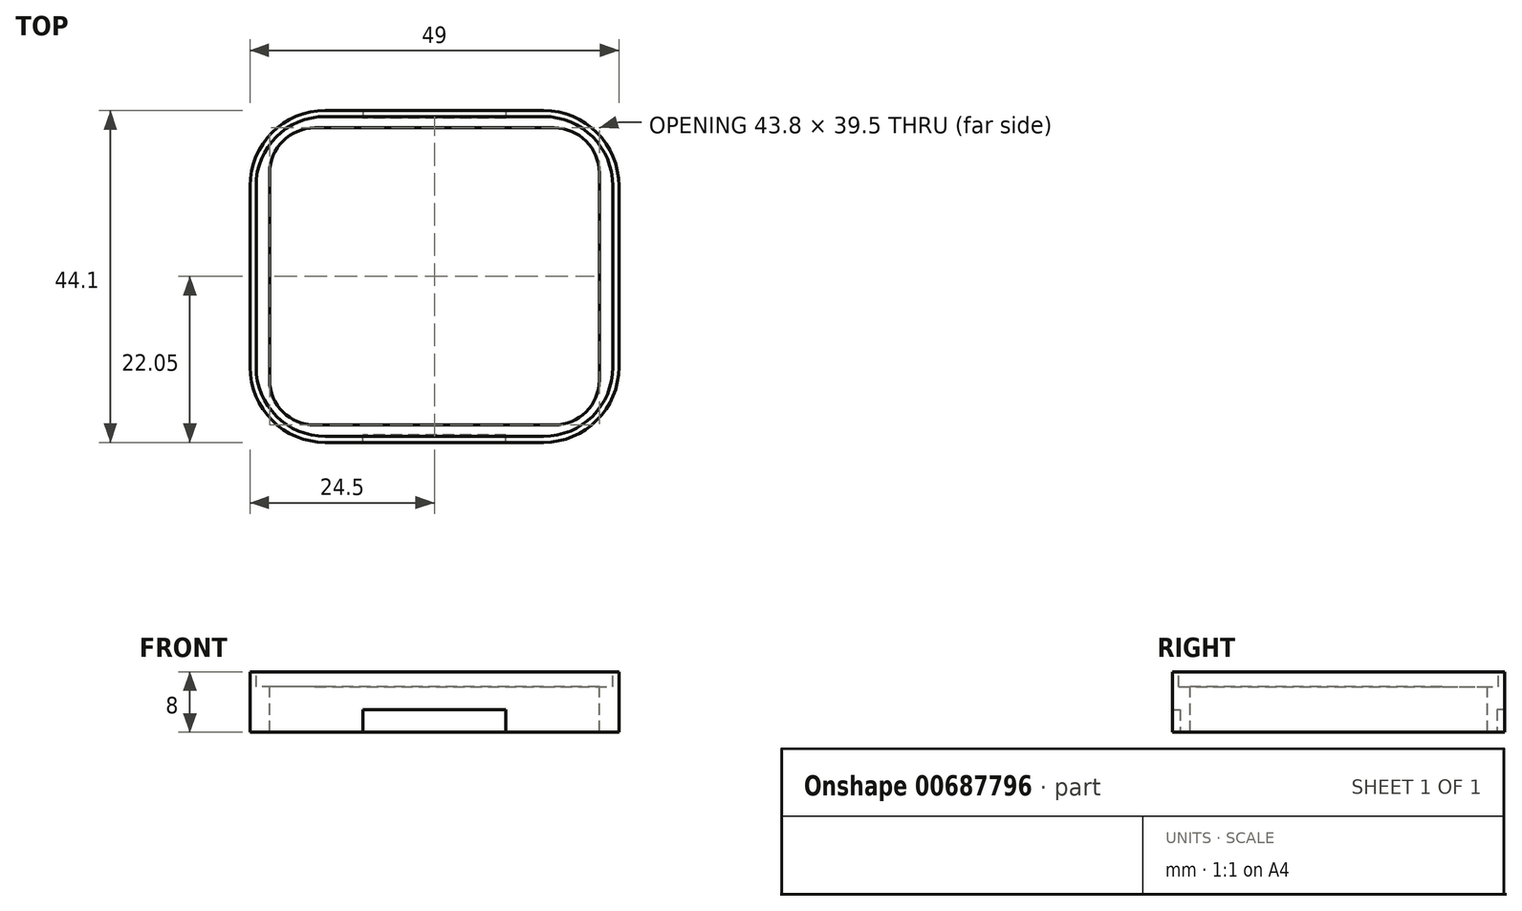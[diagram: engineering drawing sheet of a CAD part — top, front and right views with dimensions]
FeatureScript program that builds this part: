
annotation { "Feature Type Name" : "Feature", "Feature Type Description" : "" }
export const myFeature = defineFeature(function(context is Context, id is Id, definition is map)
    precondition{}
    {
        {
            var Q0;
            Q0=qCreatedBy(makeId("Top.planeOp"),FACE);
            var sketch = newSketch(context, id + "F0", { "sketchPlane" : qUnion([Q0])});
            skLineSegment(sketch, "E0.bottom", {"start": v(14.5, -22.05) * mm, "end": v(-14.5, -22.05) * mm});
            skLineSegment(sketch, "E0.top", {"start": v(14.5, 22.05) * mm, "end": v(-14.5, 22.05) * mm});
            skLineSegment(sketch, "E0.left", {"start": v(24.5, -12.05) * mm, "end": v(24.5, 12.05) * mm});
            skLineSegment(sketch, "E0.right", {"start": v(-24.5, -12.05) * mm, "end": v(-24.5, 12.05) * mm});
            skPoint(sketch, "E0.middle", {"position": v(0, 0) * mm});
            skPoint(sketch, "E1.visualSharp", {"position": v(-24.5, 22.05) * mm});
            skArc(sketch, "E1.filletArc", {"start": v(-14.5, 22.05) * mm, "mid": v(-21.57, 19.12) * mm, "end": v(-24.5, 12.05) * mm});
            skPoint(sketch, "E2.visualSharp", {"position": v(24.5, 22.05) * mm});
            skArc(sketch, "E2.filletArc", {"start": v(24.5, 12.05) * mm, "mid": v(21.57, 19.12) * mm, "end": v(14.5, 22.05) * mm});
            skPoint(sketch, "E3.visualSharp", {"position": v(24.5, -22.05) * mm});
            skArc(sketch, "E3.filletArc", {"start": v(14.5, -22.05) * mm, "mid": v(21.57, -19.12) * mm, "end": v(24.5, -12.05) * mm});
            skPoint(sketch, "E4.visualSharp", {"position": v(-24.5, -22.05) * mm});
            skArc(sketch, "E4.filletArc", {"start": v(-24.5, -12.05) * mm, "mid": v(-21.57, -19.12) * mm, "end": v(-14.5, -22.05) * mm});
            skSolve(sketch);
        }
        {
            var Q0;
            Q0=makeQuery(id+"F0.imprint","IMPRINT",FACE,{"disambiguationData":[TD([[makeQuery(id+"F0.imprint","IMPRINT",EDGE,{"derivedFrom":sQuery(id+"F0.wireOp",EDGE,"E0.bottom")}),-1.0]])]});
            var Q1;
            Q1=sQuery(id+"F0.wireOp",EDGE,"E0.top");
            var Q2;
            Q2=sQuery(id+"F0.wireOp",EDGE,"E1.filletArc");
            var Q3;
            Q3=sQuery(id+"F0.wireOp",EDGE,"E0.right");
            var Q4;
            Q4=sQuery(id+"F0.wireOp",EDGE,"E4.filletArc");
            var Q5;
            Q5=sQuery(id+"F0.wireOp",EDGE,"E0.bottom");
            var Q6;
            Q6=sQuery(id+"F0.wireOp",EDGE,"E3.filletArc");
            var Q7;
            Q7=sQuery(id+"F0.wireOp",EDGE,"E2.filletArc");
            var Q8;
            Q8=sQuery(id+"F0.wireOp",EDGE,"E0.left");
            extrude(context, id + "F1", {"entities" : qUnion([Q0]), "surfaceEntities" : qUnion([Q1, Q2, Q3, Q4, Q5, Q6, Q7, Q8]), "depth" : 8 * mm, "offsetDistance" : 25 * mm});
        }
        {
            var Q0;
            Q0=makeQuery(id+"F1.opExtrude","CAP_FACE",FACE,{"disambiguationData":[OSD([sQuery(id+"F0.wireOp",EDGE,"E0.bottom"),sQuery(id+"F0.wireOp",EDGE,"E0.top"),sQuery(id+"F0.wireOp",EDGE,"E0.left"),sQuery(id+"F0.wireOp",EDGE,"E0.right"),sQuery(id+"F0.wireOp",EDGE,"E1.filletArc"),sQuery(id+"F0.wireOp",EDGE,"E2.filletArc"),sQuery(id+"F0.wireOp",EDGE,"E3.filletArc"),sQuery(id+"F0.wireOp",EDGE,"E4.filletArc")])],"isStart":false});
            var sketch = newSketch(context, id + "F2", { "sketchPlane" : qUnion([Q0])});
            skLineSegment(sketch, "E5.bottom", {"start": v(15.9, -19.75) * mm, "end": v(-15.9, -19.75) * mm});
            skLineSegment(sketch, "E5.top", {"start": v(15.9, 19.75) * mm, "end": v(-15.9, 19.75) * mm});
            skLineSegment(sketch, "E5.left", {"start": v(21.9, -13.75) * mm, "end": v(21.9, 13.75) * mm});
            skLineSegment(sketch, "E5.right", {"start": v(-21.9, -13.75) * mm, "end": v(-21.9, 13.75) * mm});
            skPoint(sketch, "E5.middle", {"position": v(0, 0) * mm});
            skPoint(sketch, "E6.visualSharp", {"position": v(-21.9, 19.75) * mm});
            skArc(sketch, "E6.filletArc", {"start": v(-15.9, 19.75) * mm, "mid": v(-20.14, 18) * mm, "end": v(-21.9, 13.75) * mm});
            skPoint(sketch, "E7.visualSharp", {"position": v(21.9, 19.75) * mm});
            skArc(sketch, "E7.filletArc", {"start": v(21.9, 13.75) * mm, "mid": v(20.14, 18) * mm, "end": v(15.9, 19.75) * mm});
            skPoint(sketch, "E8.visualSharp", {"position": v(21.9, -19.75) * mm});
            skArc(sketch, "E8.filletArc", {"start": v(15.9, -19.75) * mm, "mid": v(20.14, -18) * mm, "end": v(21.9, -13.75) * mm});
            skPoint(sketch, "E9.visualSharp", {"position": v(-21.9, -19.75) * mm});
            skArc(sketch, "E9.filletArc", {"start": v(-21.9, -13.75) * mm, "mid": v(-20.14, -18) * mm, "end": v(-15.9, -19.75) * mm});
            skSolve(sketch);
        }
        {
            var Q0;
            Q0=makeQuery(id+"F2.imprint","IMPRINT",FACE,{"disambiguationData":[TD([[makeQuery(id+"F2.imprint","IMPRINT",EDGE,{"derivedFrom":sQuery(id+"F2.wireOp",EDGE,"E5.bottom")}),-1.0]])]});
            extrude(context, id + "F3", {"entities" : qUnion([Q0]), "operationType" : NewBodyOperationType.REMOVE, "endBound" : BoundingType.THROUGH_ALL, "oppositeDirection" : true, "depth" : 25 * mm, "offsetDistance" : 25 * mm});
        }
        {
            var Q0;
            Q0=makeQuery(id+"F1.opExtrude","CAP_FACE",FACE,{"disambiguationData":[OSD([sQuery(id+"F0.wireOp",EDGE,"E0.bottom"),sQuery(id+"F0.wireOp",EDGE,"E0.top"),sQuery(id+"F0.wireOp",EDGE,"E0.left"),sQuery(id+"F0.wireOp",EDGE,"E0.right"),sQuery(id+"F0.wireOp",EDGE,"E1.filletArc"),sQuery(id+"F0.wireOp",EDGE,"E2.filletArc"),sQuery(id+"F0.wireOp",EDGE,"E3.filletArc"),sQuery(id+"F0.wireOp",EDGE,"E4.filletArc")])],"isStart":false});
            var sketch = newSketch(context, id + "F4", { "sketchPlane" : qUnion([Q0])});
            skLineSegment(sketch, "E10.0", {"start": v(23.7, -12.05) * mm, "end": v(23.7, 12.05) * mm});
            skArc(sketch, "E10.1", {"start": v(14.5, -21.25) * mm, "mid": v(21, -18.56) * mm, "end": v(23.7, -12.05) * mm});
            skArc(sketch, "E10.2", {"start": v(23.7, 12.05) * mm, "mid": v(21, 18.56) * mm, "end": v(14.5, 21.25) * mm});
            skLineSegment(sketch, "E10.3", {"start": v(-14.5, -21.25) * mm, "end": v(14.5, -21.25) * mm});
            skLineSegment(sketch, "E10.4", {"start": v(14.5, 21.25) * mm, "end": v(-14.5, 21.25) * mm});
            skArc(sketch, "E10.5", {"start": v(-14.5, 21.25) * mm, "mid": v(-21, 18.56) * mm, "end": v(-23.7, 12.05) * mm});
            skLineSegment(sketch, "E10.6", {"start": v(-23.7, 12.05) * mm, "end": v(-23.7, -12.05) * mm});
            skArc(sketch, "E10.7", {"start": v(-23.7, -12.05) * mm, "mid": v(-21, -18.56) * mm, "end": v(-14.5, -21.25) * mm});
            skSolve(sketch);
        }
        {
            var Q0;
            Q0 = qSketchRegion(id + "F4", true);
            extrude(context, id + "F5", {"entities" : qUnion([Q0]), "operationType" : NewBodyOperationType.REMOVE, "oppositeDirection" : true, "depth" : 2 * mm, "offsetDistance" : 25 * mm});
        }
        {
            var Q0;
            Q0=qCreatedBy(makeId("Top.planeOp"),FACE);
            var sketch = newSketch(context, id + "F6", { "sketchPlane" : qUnion([Q0])});
            skLineSegment(sketch, "E11.bottom", {"start": v(9.5, -22.05) * mm, "end": v(-9.5, -22.05) * mm});
            skLineSegment(sketch, "E11.top", {"start": v(9.5, -21.05) * mm, "end": v(-9.5, -21.05) * mm});
            skLineSegment(sketch, "E11.left", {"start": v(9.5, -22.05) * mm, "end": v(9.5, -21.05) * mm});
            skLineSegment(sketch, "E11.right", {"start": v(-9.5, -22.05) * mm, "end": v(-9.5, -21.05) * mm});
            skPoint(sketch, "E11.middle", {"position": v(0, -21.55) * mm});
            skSolve(sketch);
        }
        {
            var Q0;
            Q0=makeQuery(id+"F6.imprint","IMPRINT",FACE,{"disambiguationData":[TD([[makeQuery(id+"F6.imprint","IMPRINT",EDGE,{"derivedFrom":sQuery(id+"F6.wireOp",EDGE,"E11.bottom")}),-1.0]])]});
            extrude(context, id + "F7", {"entities" : qUnion([Q0]), "operationType" : NewBodyOperationType.REMOVE, "depth" : 3 * mm, "offsetDistance" : 25 * mm});
        }
        {
            var Q0;
            Q0=makeQuery(id+"F1.opExtrude","CAP_FACE",FACE,{"disambiguationData":[OSD([sQuery(id+"F0.wireOp",EDGE,"E0.bottom"),sQuery(id+"F0.wireOp",EDGE,"E0.top"),sQuery(id+"F0.wireOp",EDGE,"E0.left"),sQuery(id+"F0.wireOp",EDGE,"E0.right"),sQuery(id+"F0.wireOp",EDGE,"E1.filletArc"),sQuery(id+"F0.wireOp",EDGE,"E2.filletArc"),sQuery(id+"F0.wireOp",EDGE,"E3.filletArc"),sQuery(id+"F0.wireOp",EDGE,"E4.filletArc")])],"isStart":true});
            var sketch = newSketch(context, id + "F8", { "sketchPlane" : qUnion([Q0])});
            skLineSegment(sketch, "E12.bottom", {"start": v(9.5, -22.05) * mm, "end": v(-9.5, -22.05) * mm});
            skLineSegment(sketch, "E12.top", {"start": v(9.5, -21.05) * mm, "end": v(-9.5, -21.05) * mm});
            skLineSegment(sketch, "E12.left", {"start": v(9.5, -22.05) * mm, "end": v(9.5, -21.05) * mm});
            skLineSegment(sketch, "E12.right", {"start": v(-9.5, -22.05) * mm, "end": v(-9.5, -21.05) * mm});
            skPoint(sketch, "E12.middle", {"position": v(0, -21.55) * mm});
            skSolve(sketch);
        }
        {
            var Q0;
            Q0 = qSketchRegion(id + "F8", true);
            extrude(context, id + "F9", {"entities" : qUnion([Q0]), "operationType" : NewBodyOperationType.REMOVE, "oppositeDirection" : true, "depth" : 3 * mm, "offsetDistance" : 25 * mm});
        }
    });
